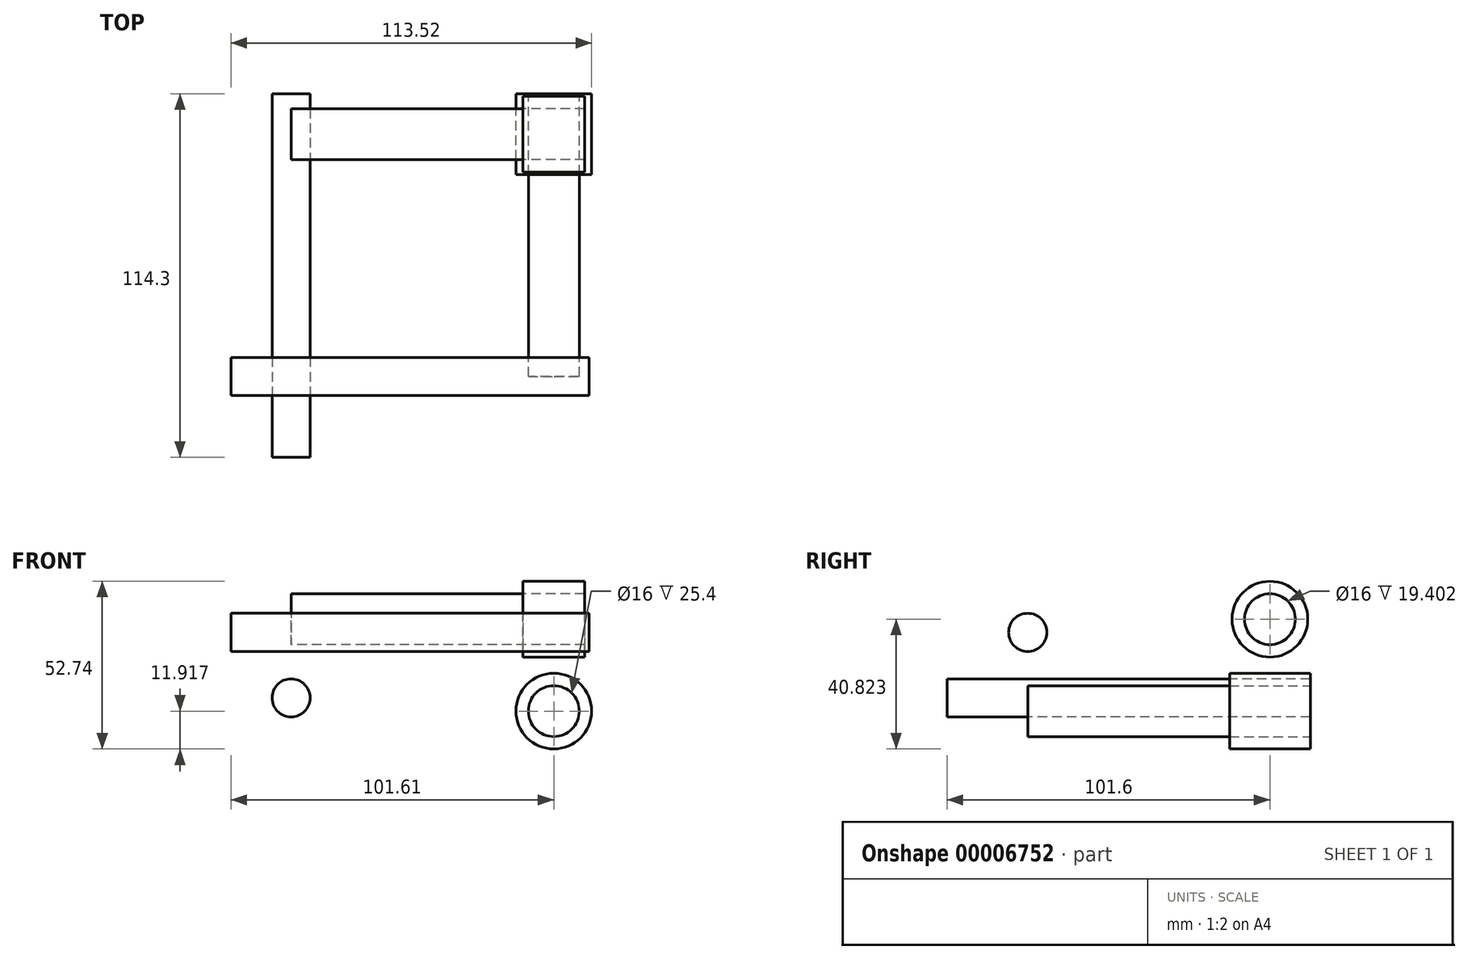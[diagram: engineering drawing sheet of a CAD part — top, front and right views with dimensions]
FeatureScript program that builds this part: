
annotation { "Feature Type Name" : "Feature", "Feature Type Description" : "" }
export const myFeature = defineFeature(function(context is Context, id is Id, definition is map)
    precondition{}
    {
        {
            var Q0;
            Q0=qCreatedBy(makeId("Front.planeOp"),FACE);
            var sketch = newSketch(context, id + "F0", { "sketchPlane" : qUnion([Q0])});
            skCircle(sketch, "E0", {"center": v(0, -14.45) * mm, "radius": 8 * mm});
            skLineSegment(sketch, "E1.bottom", {"start": v(-82.64, 22.45) * mm, "end": v(0, 22.45) * mm});
            skLineSegment(sketch, "E1.top", {"start": v(-82.64, 6.45) * mm, "end": v(0, 6.45) * mm});
            skLineSegment(sketch, "E1.left", {"start": v(-82.64, 22.45) * mm, "end": v(-82.64, 6.45) * mm});
            skLineSegment(sketch, "E1.right", {"start": v(0, 22.45) * mm, "end": v(0, 6.45) * mm});
            skLineSegment(sketch, "E2", {"start": v(0, -6.45) * mm, "end": v(0, -22.45) * mm, "construction": true});
            skLineSegment(sketch, "E3", {"start": v(0, 14.45) * mm, "end": v(0, -14.45) * mm, "construction": true});
            skLineSegment(sketch, "E4.bottom", {"start": v(9.7, 2.54) * mm, "end": v(-9.7, 2.54) * mm});
            skLineSegment(sketch, "E4.top", {"start": v(9.7, 26.37) * mm, "end": v(-9.7, 26.37) * mm});
            skLineSegment(sketch, "E4.left", {"start": v(9.7, 2.54) * mm, "end": v(9.7, 26.37) * mm});
            skLineSegment(sketch, "E4.right", {"start": v(-9.7, 2.54) * mm, "end": v(-9.7, 26.37) * mm});
            skPoint(sketch, "E4.middle", {"position": v(0, 14.45) * mm});
            skCircle(sketch, "E5", {"center": v(0, -14.45) * mm, "radius": 11.91 * mm});
            skLineSegment(sketch, "E6", {"start": v(0, -2.54) * mm, "end": v(0, -26.37) * mm, "construction": true});
            skLineSegment(sketch, "E7", {"start": v(-82.64, 14.45) * mm, "end": v(9.7, 14.45) * mm});
            skLineSegment(sketch, "E8", {"start": v(0, 22.45) * mm, "end": v(9.7, 22.45) * mm});
            skLineSegment(sketch, "E9", {"start": v(78.19, 31.95) * mm, "end": v(78.19, -3.05) * mm});
            skLineSegment(sketch, "E10", {"start": v(70.24, 3.05) * mm, "end": v(70.24, -31.95) * mm});
            skPoint(sketch, "E11", {"position": v(70.24, -14.45) * mm});
            skPoint(sketch, "E12", {"position": v(78.19, 14.45) * mm});
            skSolve(sketch);
        }
        {
            var Q0;
            Q0=makeQuery(id+"F0.imprint","IMPRINT",FACE,{"disambiguationData":[TD([[makeQuery(id+"F0.imprint","IMPRINT",EDGE,{"derivedFrom":sQuery(id+"F0.wireOp",EDGE,"E0")}),1.0]])]});
            extrude(context, id + "F1", {"entities" : qUnion([Q0]), "depth" : 76.2 * mm, "offsetDistance" : 25.4 * mm, "hasSecondDirection" : true, "secondDirectionOppositeDirection" : true, "secondDirectionDepth" : 12.7 * mm});
        }
        {
            var Q0;
            Q0=makeQuery(id+"F0.imprint","IMPRINT",FACE,{"disambiguationData":[TD([[makeQuery(id+"F0.imprint","IMPRINT",EDGE,{"derivedFrom":sQuery(id+"F0.wireOp",EDGE,"E0")}),-1.0]])]});
            extrude(context, id + "F2", {"entities" : qUnion([Q0]), "endBound" : BoundingType.SYMMETRIC, "depth" : 25.4 * mm, "offsetDistance" : 25.4 * mm});
        }
        {
            var Q0;
            {var subQ0=sQuery(id+"F0.wireOp",EDGE,"E1.right");var subQ1=sQuery(id+"F0.wireOp",EDGE,"E1.bottom");var subQ2=makeQuery(id+"F0.imprint","INTERSECT",VERTEX,{"derivedFrom":[subQ1,subQ0]});Q0=makeQuery(id+"F0.imprint","IMPRINT",FACE,{"disambiguationData":[TD([[makeQuery(id+"F0.imprint","IMPRINT",EDGE,{"disambiguationData":[TD([[subQ2,1.0]])],"derivedFrom":subQ1}),-1.0]])]});}
            var Q1;
            {var subQ0=sQuery(id+"F0.wireOp",EDGE,"E1.left");var subQ1=sQuery(id+"F0.wireOp",EDGE,"E1.bottom");var subQ2=makeQuery(id+"F0.imprint","INTERSECT",VERTEX,{"derivedFrom":[subQ1,subQ0]});Q1=makeQuery(id+"F0.imprint","IMPRINT",FACE,{"disambiguationData":[TD([[makeQuery(id+"F0.imprint","IMPRINT",EDGE,{"disambiguationData":[TD([[subQ2,-1.0]])],"derivedFrom":subQ1}),-1.0]])]});}
            var Q2;
            {var subQ0=sQuery(id+"F0.wireOp",EDGE,"E8");Q2=makeQuery(id+"F0.imprint","IMPRINT",FACE,{"disambiguationData":[TD([[makeQuery(id+"F0.imprint","IMPRINT",EDGE,{"derivedFrom":subQ0}),-1.0]])]});}
            var Q3;
            Q3=sQuery(id+"F0.wireOp",EDGE,"E7");
            revolve(context, id + "F3", {"surfaceOperationType" : NewSurfaceOperationType.NEW, "entities" : qUnion([Q0, Q1, Q2]), "axis" : qUnion([Q3]), "revolveType" : RevolveType.FULL});
        }
        {
            var Q0;
            {var subQ0=sQuery(id+"F0.wireOp",EDGE,"E4.top");Q0=makeQuery(id+"F0.imprint","IMPRINT",FACE,{"disambiguationData":[TD([[makeQuery(id+"F0.imprint","IMPRINT",EDGE,{"derivedFrom":subQ0}),1.0]])]});}
            var Q1;
            Q1=sQuery(id+"F0.wireOp",EDGE,"E7");
            revolve(context, id + "F4", {"surfaceOperationType" : NewSurfaceOperationType.NEW, "entities" : qUnion([Q0]), "axis" : qUnion([Q1]), "revolveType" : RevolveType.FULL});
        }
        {
            var Q0;
            Q0=makeQuery(id+"F1.opExtrude","CAP_FACE",FACE,{"disambiguationData":[OSD([sQuery(id+"F0.wireOp",EDGE,"E0")])],"isStart":false});
            var sketch = newSketch(context, id + "F5", { "sketchPlane" : qUnion([Q0])});
            skLineSegment(sketch, "E13.bottom", {"start": v(11.14, 16.31) * mm, "end": v(-101.6, 16.31) * mm});
            skLineSegment(sketch, "E13.top", {"start": v(11.14, 4.31) * mm, "end": v(-101.6, 4.31) * mm});
            skLineSegment(sketch, "E13.left", {"start": v(11.14, 16.31) * mm, "end": v(11.14, 4.31) * mm});
            skLineSegment(sketch, "E13.right", {"start": v(-101.6, 16.31) * mm, "end": v(-101.6, 4.31) * mm});
            skCircle(sketch, "E14", {"center": v(-82.64, -10.31) * mm, "radius": 6 * mm});
            skLineSegment(sketch, "E15", {"start": v(-82.64, -4.31) * mm, "end": v(-82.64, -16.31) * mm, "construction": true});
            skCircle(sketch, "E16.0", {"center": v(0, -14.45) * mm, "radius": 8 * mm});
            skLineSegment(sketch, "E17.0", {"start": v(-82.64, 6.45) * mm, "end": v(-82.64, 22.45) * mm});
            skLineSegment(sketch, "E18", {"start": v(0, -6.45) * mm, "end": v(0, 4.31) * mm, "construction": true});
            skLineSegment(sketch, "E19", {"start": v(-101.6, 10.31) * mm, "end": v(11.14, 10.31) * mm});
            skLineSegment(sketch, "E20", {"start": v(-82.64, -4.31) * mm, "end": v(-82.64, 6.45) * mm, "construction": true});
            skSolve(sketch);
        }
        {
            var Q0;
            Q0=makeQuery(id+"F5.imprint","IMPRINT",FACE,{"disambiguationData":[TD([[makeQuery(id+"F5.imprint","IMPRINT",EDGE,{"derivedFrom":sQuery(id+"F5.wireOp",EDGE,"E14")}),1.0]])]});
            extrude(context, id + "F6", {"entities" : qUnion([Q0]), "oppositeDirection" : true, "depth" : 88.9 * mm, "offsetDistance" : 25.4 * mm, "hasSecondDirection" : true, "secondDirectionOppositeDirection" : false, "secondDirectionDepth" : 25.4 * mm});
        }
        {
            var Q0;
            {var subQ0=sQuery(id+"F5.wireOp",EDGE,"E13.bottom");Q0=makeQuery(id+"F5.imprint","IMPRINT",FACE,{"disambiguationData":[TD([[makeQuery(id+"F5.imprint","IMPRINT",EDGE,{"derivedFrom":subQ0}),1.0]])]});}
            var Q1;
            Q1=sQuery(id+"F5.wireOp",EDGE,"E19");
            revolve(context, id + "F7", {"surfaceOperationType" : NewSurfaceOperationType.NEW, "entities" : qUnion([Q0]), "axis" : qUnion([Q1]), "revolveType" : RevolveType.FULL});
        }
    });
